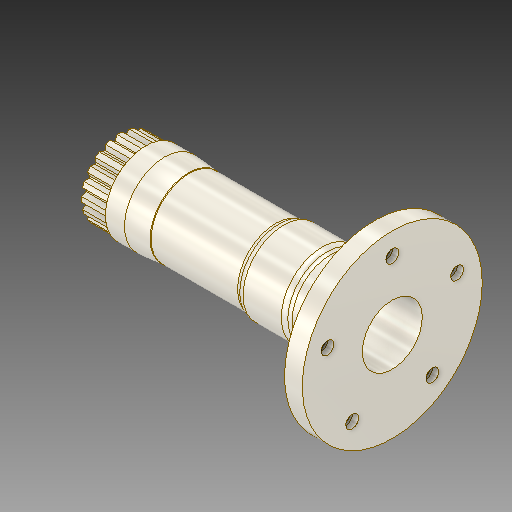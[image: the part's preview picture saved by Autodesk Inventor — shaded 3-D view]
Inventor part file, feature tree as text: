
AUTODESK INVENTOR PART (.ipt)
format: ipt  version: 2019 (Build 230136000, 136)  size: 359,936 bytes
history: native  units: mm
features: sketch x4, fillet x2, extrude x2, revolve x1, plane x1, hole x1, pattern_circular x1
ambient origin geometry x8: Origin, YZ Plane, XZ Plane, XY Plane, X Axis, Y Axis, Z Axis, Center Point
bodies: Solid1 (feature_tree)
feature tree (12):
  revolve  "Revolution1"  [1 undecoded]
  fillet  "Fillet1"  Radius=3.75mm
  extrude  "Extrusion1"  Depth=3.0mm
  fillet  "Fillet2"  Radius=52.5mm
  plane  "Work Plane1"
  hole  "Hole1"  [1 undecoded]
  pattern_circular  "Circular Pattern1"  Angle=90.0deg  [1 undecoded]
  extrude  "Extrusion2"  Depth=3.0mm
  sketch  "Sketch1"  dims[d0=100.0mm d1=22.0mm d2=3.75mm]
  sketch  "Sketch2"  dims[d3=16.5mm d9=3.0mm d10=52.5mm]
  sketch  "Sketch3"  dims[d11=58.0mm d12=18.5mm]
  sketch  "Sketch4"  dims[d13=4.0mm d14=90.0deg d15=3.0mm d16=2.0mm d17=66.0mm d18=6.5mm d19=0.0mm d20=25.0mm d21=-1.05mm d22=6.0mm d23=5.984mm d24=11.4mm d25=2.0mm d26=90.0deg d27=5.0mm d28=19.198622mm d29=50.0mm d30=360.0deg d32=25.0mm d33=1.8mm d34=14.0mm d35=20.245819mm d36=200.0mm d38=360.0deg d40=9.5mm d41=0.0mm]
note: 3 required parameter values undecoded (feature->parameter linkage not recoverable at this tier; creation-order binding heuristic only, values carry confidence <= 0.55)